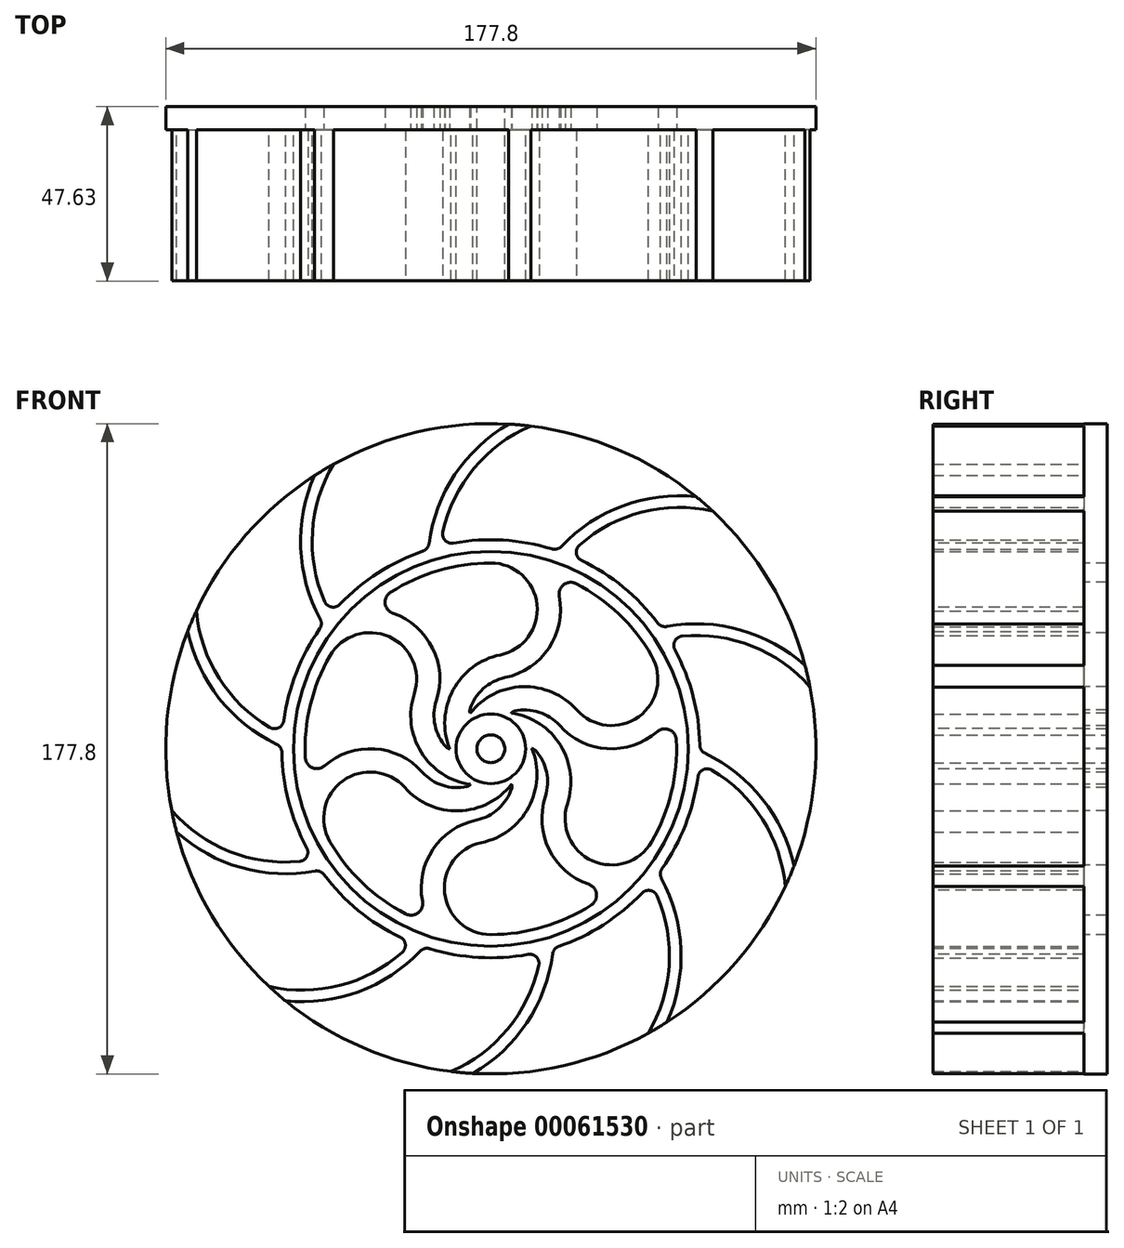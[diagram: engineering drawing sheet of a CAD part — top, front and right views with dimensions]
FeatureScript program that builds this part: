
annotation { "Feature Type Name" : "Feature", "Feature Type Description" : "" }
export const myFeature = defineFeature(function(context is Context, id is Id, definition is map)
    precondition{}
    {
        {
            var Q0;
            Q0=qCreatedBy(makeId("Front.planeOp"),FACE);
            var sketch = newSketch(context, id + "F0", { "sketchPlane" : qUnion([Q0])});
            skCircle(sketch, "E0", {"center": v(0, 0) * mm, "radius": 88.9 * mm});
            skSolve(sketch);
        }
        {
            var Q0;
            Q0=makeQuery(id+"F0.imprint","IMPRINT",FACE,{"disambiguationData":[TD([[makeQuery(id+"F0.imprint","IMPRINT",EDGE,{"derivedFrom":sQuery(id+"F0.wireOp",EDGE,"E0")}),1.0]])]});
            extrude(context, id + "F1", {"entities" : qUnion([Q0]), "depth" : 6.35 * mm});
        }
        {
            var Q0;
            Q0=makeQuery(id+"F1.opExtrude","CAP_FACE",FACE,{"disambiguationData":[OSD([sQuery(id+"F0.wireOp",EDGE,"E0")])],"isStart":false});
            var sketch = newSketch(context, id + "F2", { "sketchPlane" : qUnion([Q0])});
            skCircle(sketch, "E1", {"center": v(0, 0) * mm, "radius": 57.15 * mm});
            skCircle(sketch, "E2", {"center": v(0, 0) * mm, "radius": 53.98 * mm});
            skSolve(sketch);
        }
        {
            var Q0;
            Q0 = qSketchRegion(id + "F2", true);
            extrude(context, id + "F3", {"entities" : qUnion([Q0]), "operationType" : NewBodyOperationType.ADD, "depth" : 41.27 * mm});
        }
        {
            var Q0;
            {var subQ0=sQuery(id+"F0.wireOp",EDGE,"E0");Q0=makeQuery(id+"F3.boolean.opBoolean","SPLIT",FACE,{"disambiguationData":[TD([makeQuery(id+"F1.opExtrude","SWEPT_FACE",FACE,{"disambiguationData":[OSD([subQ0])]})])],"derivedFrom":makeQuery(id+"F1.opExtrude","CAP_FACE",FACE,{"disambiguationData":[OSD([subQ0])],"isStart":false})});}
            var sketch = newSketch(context, id + "F4", { "sketchPlane" : qUnion([Q0])});
            skArc(sketch, "E3", {"start": v(80.54, -37.63) * mm, "mid": v(72.26, -16.34) * mm, "end": v(53.9, -2.7) * mm});
            skArc(sketch, "E4", {"start": v(82.9, -32.09) * mm, "mid": v(72.74, -11.92) * mm, "end": v(53.97, 0.64) * mm});
            skArc(sketch, "E5.0", {"start": v(53.9, -2.7) * mm, "mid": v(53.97, -1.03) * mm, "end": v(53.97, 0.64) * mm});
            skArc(sketch, "E6.0", {"start": v(80.54, -37.63) * mm, "mid": v(81.77, -34.88) * mm, "end": v(82.9, -32.09) * mm});
            skArc(sketch, "E7.1.0", {"start": v(87.28, 16.9) * mm, "mid": v(68.06, 29.26) * mm, "end": v(45.2, 29.5) * mm});
            skArc(sketch, "E7.1.1", {"start": v(85.93, 22.77) * mm, "mid": v(65.85, 33.1) * mm, "end": v(43.29, 32.24) * mm});
            skArc(sketch, "E7.1.2", {"start": v(87.28, 16.9) * mm, "mid": v(86.66, 19.84) * mm, "end": v(85.93, 22.77) * mm});
            skArc(sketch, "E7.1.3", {"start": v(45.2, 29.5) * mm, "mid": v(44.27, 30.88) * mm, "end": v(43.29, 32.24) * mm});
            skArc(sketch, "E7.2.0", {"start": v(60.68, 64.97) * mm, "mid": v(37.86, 63.67) * mm, "end": v(19.24, 50.43) * mm});
            skArc(sketch, "E7.2.1", {"start": v(56.14, 68.93) * mm, "mid": v(33.82, 65.5) * mm, "end": v(16.07, 51.53) * mm});
            skArc(sketch, "E7.2.2", {"start": v(60.68, 64.97) * mm, "mid": v(58.44, 66.99) * mm, "end": v(56.14, 68.93) * mm});
            skArc(sketch, "E7.2.3", {"start": v(19.24, 50.43) * mm, "mid": v(17.66, 51) * mm, "end": v(16.07, 51.53) * mm});
            skArc(sketch, "E7.3.0", {"start": v(10.9, 88.23) * mm, "mid": v(-6.8, 73.77) * mm, "end": v(-14.08, 52.1) * mm});
            skArc(sketch, "E7.3.1", {"start": v(4.9, 88.76) * mm, "mid": v(-11.14, 72.86) * mm, "end": v(-17.29, 51.13) * mm});
            skArc(sketch, "E7.3.2", {"start": v(10.9, 88.23) * mm, "mid": v(7.9, 88.55) * mm, "end": v(4.9, 88.76) * mm});
            skArc(sketch, "E7.3.3", {"start": v(-14.08, 52.1) * mm, "mid": v(-15.7, 51.64) * mm, "end": v(-17.29, 51.13) * mm});
            skArc(sketch, "E7.4.0", {"start": v(-43.04, 77.79) * mm, "mid": v(-48.85, 55.69) * mm, "end": v(-42.02, 33.88) * mm});
            skArc(sketch, "E7.4.1", {"start": v(-48.21, 74.7) * mm, "mid": v(-51.84, 52.4) * mm, "end": v(-44.04, 31.2) * mm});
            skArc(sketch, "E7.4.2", {"start": v(-43.04, 77.79) * mm, "mid": v(-45.65, 76.28) * mm, "end": v(-48.21, 74.7) * mm});
            skArc(sketch, "E7.4.3", {"start": v(-42.02, 33.88) * mm, "mid": v(-43.05, 32.56) * mm, "end": v(-44.04, 31.2) * mm});
            skArc(sketch, "E7.5.0", {"start": v(-80.54, 37.63) * mm, "mid": v(-72.26, 16.34) * mm, "end": v(-53.9, 2.7) * mm});
            skArc(sketch, "E7.5.1", {"start": v(-82.9, 32.09) * mm, "mid": v(-72.74, 11.92) * mm, "end": v(-53.97, -0.64) * mm});
            skArc(sketch, "E7.5.2", {"start": v(-80.54, 37.63) * mm, "mid": v(-81.77, 34.88) * mm, "end": v(-82.9, 32.09) * mm});
            skArc(sketch, "E7.5.3", {"start": v(-53.9, 2.7) * mm, "mid": v(-53.97, 1.03) * mm, "end": v(-53.97, -0.64) * mm});
            skArc(sketch, "E7.6.0", {"start": v(-87.28, -16.9) * mm, "mid": v(-68.06, -29.26) * mm, "end": v(-45.2, -29.5) * mm});
            skArc(sketch, "E7.6.1", {"start": v(-85.93, -22.77) * mm, "mid": v(-65.85, -33.1) * mm, "end": v(-43.29, -32.24) * mm});
            skArc(sketch, "E7.6.2", {"start": v(-87.28, -16.9) * mm, "mid": v(-86.66, -19.84) * mm, "end": v(-85.93, -22.77) * mm});
            skArc(sketch, "E7.6.3", {"start": v(-45.2, -29.5) * mm, "mid": v(-44.27, -30.88) * mm, "end": v(-43.29, -32.24) * mm});
            skArc(sketch, "E7.7.0", {"start": v(-60.68, -64.97) * mm, "mid": v(-37.86, -63.67) * mm, "end": v(-19.24, -50.43) * mm});
            skArc(sketch, "E7.7.1", {"start": v(-56.14, -68.93) * mm, "mid": v(-33.82, -65.5) * mm, "end": v(-16.07, -51.53) * mm});
            skArc(sketch, "E7.7.2", {"start": v(-60.68, -64.97) * mm, "mid": v(-58.44, -66.99) * mm, "end": v(-56.14, -68.93) * mm});
            skArc(sketch, "E7.7.3", {"start": v(-19.24, -50.43) * mm, "mid": v(-17.66, -51) * mm, "end": v(-16.07, -51.53) * mm});
            skArc(sketch, "E7.8.0", {"start": v(-10.9, -88.23) * mm, "mid": v(6.8, -73.77) * mm, "end": v(14.08, -52.1) * mm});
            skArc(sketch, "E7.8.1", {"start": v(-4.9, -88.76) * mm, "mid": v(11.14, -72.86) * mm, "end": v(17.29, -51.13) * mm});
            skArc(sketch, "E7.8.2", {"start": v(-10.9, -88.23) * mm, "mid": v(-7.9, -88.55) * mm, "end": v(-4.9, -88.76) * mm});
            skArc(sketch, "E7.8.3", {"start": v(14.08, -52.1) * mm, "mid": v(15.7, -51.64) * mm, "end": v(17.29, -51.13) * mm});
            skArc(sketch, "E7.9.0", {"start": v(43.04, -77.79) * mm, "mid": v(48.85, -55.69) * mm, "end": v(42.02, -33.88) * mm});
            skArc(sketch, "E7.9.1", {"start": v(48.21, -74.7) * mm, "mid": v(51.84, -52.4) * mm, "end": v(44.04, -31.2) * mm});
            skArc(sketch, "E7.9.2", {"start": v(43.04, -77.79) * mm, "mid": v(45.65, -76.28) * mm, "end": v(48.21, -74.7) * mm});
            skArc(sketch, "E7.9.3", {"start": v(42.02, -33.88) * mm, "mid": v(43.05, -32.56) * mm, "end": v(44.04, -31.2) * mm});
            skSolve(sketch);
        }
        {
            var Q0;
            Q0 = qSketchRegion(id + "F4", true);
            var Q1;
            Q1=makeQuery(id+"F3.opExtrude","CAP_FACE",FACE,{"disambiguationData":[OSD([sQuery(id+"F2.wireOp",EDGE,"E1"),sQuery(id+"F2.wireOp",EDGE,"E2")])],"isStart":false});
            extrude(context, id + "F5", {"entities" : qUnion([Q0]), "operationType" : NewBodyOperationType.ADD, "endBound" : BoundingType.UP_TO_SURFACE, "endBoundEntityFace" : qUnion([Q1]), "depth" : 25.4 * mm});
        }
        {
            var Q0;
            Q0=makeQuery(id+"F3.boolean.opBoolean","SPLIT",FACE,{"disambiguationData":[TD([makeQuery(id+"F3.opExtrude","SWEPT_FACE",FACE,{"disambiguationData":[OSD([sQuery(id+"F2.wireOp",EDGE,"E2")])]})])],"derivedFrom":makeQuery(id+"F1.opExtrude","CAP_FACE",FACE,{"disambiguationData":[OSD([sQuery(id+"F0.wireOp",EDGE,"E0")])],"isStart":false})});
            var sketch = newSketch(context, id + "F6", { "sketchPlane" : qUnion([Q0])});
            skCircle(sketch, "E8", {"center": v(0, 0) * mm, "radius": 3.81 * mm});
            skCircle(sketch, "E9", {"center": v(0, 0) * mm, "radius": 9.53 * mm});
            skSolve(sketch);
        }
        {
            var Q0;
            Q0 = qSketchRegion(id + "F6", true);
            var Q1;
            {var subQ0=sQuery(id+"F2.wireOp",EDGE,"E2");var subQ1=sQuery(id+"F2.wireOp",EDGE,"E1");Q1=makeQuery(id+"F5.boolean.opBoolean","MERGE",FACE,{"derivedFrom":[makeQuery(id+"F3.opExtrude","CAP_FACE",FACE,{"disambiguationData":[OSD([subQ1,subQ0])],"isStart":false}),makeQuery(id+"F5.opExtrude","CAP_FACE",FACE,{"disambiguationData":[OSD([subQ1,subQ0]),ownerDisambiguation([makeQuery(id+"F5.opExtrude","SWEPT_BODY",BODY,{"disambiguationData":[OSD([sQuery(id+"F4.wireOp",EDGE,"E3"),sQuery(id+"F4.wireOp",EDGE,"E4"),sQuery(id+"F4.wireOp",EDGE,"E5.0"),sQuery(id+"F4.wireOp",EDGE,"E6.0")])]})])],"isStart":false}),makeQuery(id+"F5.opExtrude","CAP_FACE",FACE,{"disambiguationData":[OSD([subQ1,subQ0]),ownerDisambiguation([makeQuery(id+"F5.opExtrude","SWEPT_BODY",BODY,{"disambiguationData":[OSD([sQuery(id+"F4.wireOp",EDGE,"E7.1.0"),sQuery(id+"F4.wireOp",EDGE,"E7.1.1"),sQuery(id+"F4.wireOp",EDGE,"E7.1.2"),sQuery(id+"F4.wireOp",EDGE,"E7.1.3")])]})])],"isStart":false}),makeQuery(id+"F5.opExtrude","CAP_FACE",FACE,{"disambiguationData":[OSD([subQ1,subQ0]),ownerDisambiguation([makeQuery(id+"F5.opExtrude","SWEPT_BODY",BODY,{"disambiguationData":[OSD([sQuery(id+"F4.wireOp",EDGE,"E7.2.0"),sQuery(id+"F4.wireOp",EDGE,"E7.2.1"),sQuery(id+"F4.wireOp",EDGE,"E7.2.2"),sQuery(id+"F4.wireOp",EDGE,"E7.2.3")])]})])],"isStart":false}),makeQuery(id+"F5.opExtrude","CAP_FACE",FACE,{"disambiguationData":[OSD([subQ1,subQ0]),ownerDisambiguation([makeQuery(id+"F5.opExtrude","SWEPT_BODY",BODY,{"disambiguationData":[OSD([sQuery(id+"F4.wireOp",EDGE,"E7.3.0"),sQuery(id+"F4.wireOp",EDGE,"E7.3.1"),sQuery(id+"F4.wireOp",EDGE,"E7.3.2"),sQuery(id+"F4.wireOp",EDGE,"E7.3.3")])]})])],"isStart":false}),makeQuery(id+"F5.opExtrude","CAP_FACE",FACE,{"disambiguationData":[OSD([subQ1,subQ0]),ownerDisambiguation([makeQuery(id+"F5.opExtrude","SWEPT_BODY",BODY,{"disambiguationData":[OSD([sQuery(id+"F4.wireOp",EDGE,"E7.4.0"),sQuery(id+"F4.wireOp",EDGE,"E7.4.1"),sQuery(id+"F4.wireOp",EDGE,"E7.4.2"),sQuery(id+"F4.wireOp",EDGE,"E7.4.3")])]})])],"isStart":false}),makeQuery(id+"F5.opExtrude","CAP_FACE",FACE,{"disambiguationData":[OSD([subQ1,subQ0]),ownerDisambiguation([makeQuery(id+"F5.opExtrude","SWEPT_BODY",BODY,{"disambiguationData":[OSD([sQuery(id+"F4.wireOp",EDGE,"E7.5.0"),sQuery(id+"F4.wireOp",EDGE,"E7.5.1"),sQuery(id+"F4.wireOp",EDGE,"E7.5.2"),sQuery(id+"F4.wireOp",EDGE,"E7.5.3")])]})])],"isStart":false}),makeQuery(id+"F5.opExtrude","CAP_FACE",FACE,{"disambiguationData":[OSD([subQ1,subQ0]),ownerDisambiguation([makeQuery(id+"F5.opExtrude","SWEPT_BODY",BODY,{"disambiguationData":[OSD([sQuery(id+"F4.wireOp",EDGE,"E7.6.0"),sQuery(id+"F4.wireOp",EDGE,"E7.6.1"),sQuery(id+"F4.wireOp",EDGE,"E7.6.2"),sQuery(id+"F4.wireOp",EDGE,"E7.6.3")])]})])],"isStart":false}),makeQuery(id+"F5.opExtrude","CAP_FACE",FACE,{"disambiguationData":[OSD([subQ1,subQ0]),ownerDisambiguation([makeQuery(id+"F5.opExtrude","SWEPT_BODY",BODY,{"disambiguationData":[OSD([sQuery(id+"F4.wireOp",EDGE,"E7.7.0"),sQuery(id+"F4.wireOp",EDGE,"E7.7.1"),sQuery(id+"F4.wireOp",EDGE,"E7.7.2"),sQuery(id+"F4.wireOp",EDGE,"E7.7.3")])]})])],"isStart":false}),makeQuery(id+"F5.opExtrude","CAP_FACE",FACE,{"disambiguationData":[OSD([subQ1,subQ0]),ownerDisambiguation([makeQuery(id+"F5.opExtrude","SWEPT_BODY",BODY,{"disambiguationData":[OSD([sQuery(id+"F4.wireOp",EDGE,"E7.8.0"),sQuery(id+"F4.wireOp",EDGE,"E7.8.1"),sQuery(id+"F4.wireOp",EDGE,"E7.8.2"),sQuery(id+"F4.wireOp",EDGE,"E7.8.3")])]})])],"isStart":false}),makeQuery(id+"F5.opExtrude","CAP_FACE",FACE,{"disambiguationData":[OSD([subQ1,subQ0]),ownerDisambiguation([makeQuery(id+"F5.opExtrude","SWEPT_BODY",BODY,{"disambiguationData":[OSD([sQuery(id+"F4.wireOp",EDGE,"E7.9.0"),sQuery(id+"F4.wireOp",EDGE,"E7.9.1"),sQuery(id+"F4.wireOp",EDGE,"E7.9.2"),sQuery(id+"F4.wireOp",EDGE,"E7.9.3")])]})])],"isStart":false})]});}
            extrude(context, id + "F7", {"entities" : qUnion([Q0]), "operationType" : NewBodyOperationType.ADD, "endBound" : BoundingType.UP_TO_SURFACE, "endBoundEntityFace" : qUnion([Q1]), "depth" : 25.4 * mm});
        }
        {
            var Q0;
            {var subQ0=makeQuery(id+"F3.opExtrude","SWEPT_FACE",FACE,{"disambiguationData":[OSD([sQuery(id+"F2.wireOp",EDGE,"E2")])]});Q0=makeQuery(id+"F7.boolean.opBoolean","SPLIT",FACE,{"disambiguationData":[TD([subQ0])],"derivedFrom":makeQuery(id+"F3.boolean.opBoolean","SPLIT",FACE,{"disambiguationData":[TD([subQ0])],"derivedFrom":makeQuery(id+"F1.opExtrude","CAP_FACE",FACE,{"disambiguationData":[OSD([sQuery(id+"F0.wireOp",EDGE,"E0")])],"isStart":false})})});}
            var sketch = newSketch(context, id + "F8", { "sketchPlane" : qUnion([Q0])});
            skCircle(sketch, "E10.0", {"center": v(0, 0) * mm, "radius": 3.81 * mm});
            skArc(sketch, "E11", {"start": v(0, 50.8) * mm, "mid": v(-14.31, 48.74) * mm, "end": v(-27.47, 42.73) * mm, "construction": true});
            skArc(sketch, "E12", {"start": v(3.87, 19.45) * mm, "mid": v(-2.1, 16.41) * mm, "end": v(-5.68, 10.77) * mm});
            skArc(sketch, "E13", {"start": v(2.58, 25.66) * mm, "mid": v(-10.33, 16.04) * mm, "end": v(-11.26, -0.03) * mm});
            skArc(sketch, "E14", {"start": v(2.58, 25.66) * mm, "mid": v(12.63, 39.4) * mm, "end": v(0, 50.8) * mm});
            skArc(sketch, "E15", {"start": v(3.87, 19.45) * mm, "mid": v(15.86, 27.54) * mm, "end": v(18.7, 41.73) * mm});
            skPoint(sketch, "E16.visualSharp", {"position": v(16.18, 48.15) * mm});
            skArc(sketch, "E16.filletArc", {"start": v(23.27, 45.16) * mm, "mid": v(19.91, 44.87) * mm, "end": v(18.7, 41.73) * mm});
            skPoint(sketch, "E17.visualSharp", {"position": v(-6.25, 7.19) * mm});
            skArc(sketch, "E17.filletArc", {"start": v(-5.68, 10.77) * mm, "mid": v(-5.75, 10.25) * mm, "end": v(-5.65, 9.73) * mm});
            skPoint(sketch, "E18.1.1", {"position": v(-33.61, 38.1) * mm});
            skArc(sketch, "E18.1.2", {"start": v(-14.9, 13.07) * mm, "mid": v(-15.26, 6.4) * mm, "end": v(-12.17, 0.46) * mm});
            skArc(sketch, "E18.1.3", {"start": v(-20.94, 15.07) * mm, "mid": v(-27.8, 30.64) * mm, "end": v(-44, 25.4) * mm});
            skArc(sketch, "E18.1.4", {"start": v(-20.94, 15.07) * mm, "mid": v(-19.06, -0.92) * mm, "end": v(-5.6, -9.76) * mm});
            skPoint(sketch, "E18.1.5", {"position": v(-9.35, -1.82) * mm});
            skArc(sketch, "E18.1.6", {"start": v(-14.9, 13.07) * mm, "mid": v(-15.92, 27.5) * mm, "end": v(-26.79, 37.06) * mm});
            skArc(sketch, "E18.1.7", {"start": v(-27.47, 42.73) * mm, "mid": v(-28.9, 39.68) * mm, "end": v(-26.79, 37.06) * mm});
            skArc(sketch, "E18.1.8", {"start": v(-12.17, 0.46) * mm, "mid": v(-11.75, 0.14) * mm, "end": v(-11.26, -0.03) * mm});
            skPoint(sketch, "E18.2.1", {"position": v(-49.8, -10.06) * mm});
            skArc(sketch, "E18.2.2", {"start": v(-18.78, -6.37) * mm, "mid": v(-13.17, -10.02) * mm, "end": v(-6.49, -10.3) * mm});
            skArc(sketch, "E18.2.3", {"start": v(-23.52, -10.6) * mm, "mid": v(-40.43, -8.76) * mm, "end": v(-44, -25.4) * mm});
            skArc(sketch, "E18.2.4", {"start": v(-23.52, -10.6) * mm, "mid": v(-8.73, -16.96) * mm, "end": v(5.65, -9.73) * mm});
            skPoint(sketch, "E18.2.5", {"position": v(-3.1, -9) * mm});
            skArc(sketch, "E18.2.6", {"start": v(-18.78, -6.37) * mm, "mid": v(-31.78, -0.04) * mm, "end": v(-45.49, -4.67) * mm});
            skArc(sketch, "E18.2.7", {"start": v(-50.74, -2.42) * mm, "mid": v(-48.82, -5.2) * mm, "end": v(-45.49, -4.67) * mm});
            skArc(sketch, "E18.2.8", {"start": v(-6.49, -10.3) * mm, "mid": v(-6, -10.1) * mm, "end": v(-5.6, -9.76) * mm});
            skPoint(sketch, "E18.3.1", {"position": v(-16.18, -48.15) * mm});
            skArc(sketch, "E18.3.2", {"start": v(-3.87, -19.45) * mm, "mid": v(2.1, -16.41) * mm, "end": v(5.68, -10.77) * mm});
            skArc(sketch, "E18.3.3", {"start": v(-2.58, -25.66) * mm, "mid": v(-12.63, -39.4) * mm, "end": v(0, -50.8) * mm});
            skArc(sketch, "E18.3.4", {"start": v(-2.58, -25.66) * mm, "mid": v(10.33, -16.04) * mm, "end": v(11.26, 0.03) * mm});
            skPoint(sketch, "E18.3.5", {"position": v(6.25, -7.19) * mm});
            skArc(sketch, "E18.3.6", {"start": v(-3.87, -19.45) * mm, "mid": v(-15.86, -27.54) * mm, "end": v(-18.7, -41.73) * mm});
            skArc(sketch, "E18.3.7", {"start": v(-23.27, -45.16) * mm, "mid": v(-19.91, -44.87) * mm, "end": v(-18.7, -41.73) * mm});
            skArc(sketch, "E18.3.8", {"start": v(5.68, -10.77) * mm, "mid": v(5.75, -10.25) * mm, "end": v(5.65, -9.73) * mm});
            skPoint(sketch, "E18.4.1", {"position": v(33.61, -38.1) * mm});
            skArc(sketch, "E18.4.2", {"start": v(14.9, -13.07) * mm, "mid": v(15.26, -6.4) * mm, "end": v(12.17, -0.46) * mm});
            skArc(sketch, "E18.4.3", {"start": v(20.94, -15.07) * mm, "mid": v(27.8, -30.64) * mm, "end": v(44, -25.4) * mm});
            skArc(sketch, "E18.4.4", {"start": v(20.94, -15.07) * mm, "mid": v(19.06, 0.92) * mm, "end": v(5.6, 9.76) * mm});
            skPoint(sketch, "E18.4.5", {"position": v(9.35, 1.82) * mm});
            skArc(sketch, "E18.4.6", {"start": v(14.9, -13.07) * mm, "mid": v(15.92, -27.5) * mm, "end": v(26.79, -37.06) * mm});
            skArc(sketch, "E18.4.7", {"start": v(27.47, -42.73) * mm, "mid": v(28.9, -39.68) * mm, "end": v(26.79, -37.06) * mm});
            skArc(sketch, "E18.4.8", {"start": v(12.17, -0.46) * mm, "mid": v(11.75, -0.14) * mm, "end": v(11.26, 0.03) * mm});
            skPoint(sketch, "E18.5.1", {"position": v(49.8, 10.06) * mm});
            skArc(sketch, "E18.5.2", {"start": v(18.78, 6.37) * mm, "mid": v(13.17, 10.02) * mm, "end": v(6.49, 10.3) * mm});
            skArc(sketch, "E18.5.3", {"start": v(23.52, 10.6) * mm, "mid": v(40.43, 8.76) * mm, "end": v(44, 25.4) * mm});
            skArc(sketch, "E18.5.4", {"start": v(23.52, 10.6) * mm, "mid": v(8.73, 16.96) * mm, "end": v(-5.65, 9.73) * mm});
            skPoint(sketch, "E18.5.5", {"position": v(3.1, 9) * mm});
            skArc(sketch, "E18.5.6", {"start": v(18.78, 6.37) * mm, "mid": v(31.78, 0.04) * mm, "end": v(45.49, 4.67) * mm});
            skArc(sketch, "E18.5.7", {"start": v(50.74, 2.42) * mm, "mid": v(48.82, 5.2) * mm, "end": v(45.49, 4.67) * mm});
            skArc(sketch, "E18.5.8", {"start": v(6.49, 10.3) * mm, "mid": v(6, 10.1) * mm, "end": v(5.6, 9.76) * mm});
            skArc(sketch, "E19", {"start": v(44, 25.4) * mm, "mid": v(35.05, 36.77) * mm, "end": v(23.27, 45.16) * mm});
            skArc(sketch, "E20.trimOffspring", {"start": v(44, -25.4) * mm, "mid": v(49.37, -11.97) * mm, "end": v(50.74, 2.42) * mm});
            skArc(sketch, "E21.trimOffspring", {"start": v(0, 50.8) * mm, "mid": v(-14.31, 48.74) * mm, "end": v(-27.47, 42.73) * mm});
            skArc(sketch, "E22.trimOffspring", {"start": v(44, 25.4) * mm, "mid": v(35.05, 36.77) * mm, "end": v(23.27, 45.16) * mm, "construction": true});
            skArc(sketch, "E23.trimOffspring", {"start": v(44, -25.4) * mm, "mid": v(49.37, -11.97) * mm, "end": v(50.74, 2.42) * mm, "construction": true});
            skArc(sketch, "E24.trimOffspring", {"start": v(0, -50.8) * mm, "mid": v(14.31, -48.74) * mm, "end": v(27.47, -42.73) * mm});
            skArc(sketch, "E25.trimOffspring", {"start": v(0, -50.8) * mm, "mid": v(14.31, -48.74) * mm, "end": v(27.47, -42.73) * mm, "construction": true});
            skArc(sketch, "E26.trimOffspring", {"start": v(-44, 25.4) * mm, "mid": v(-49.37, 11.97) * mm, "end": v(-50.74, -2.42) * mm});
            skArc(sketch, "E27.trimOffspring", {"start": v(-44, -25.4) * mm, "mid": v(-35.05, -36.77) * mm, "end": v(-23.27, -45.16) * mm});
            skArc(sketch, "E28.trimOffspring", {"start": v(-44, -25.4) * mm, "mid": v(-35.05, -36.77) * mm, "end": v(-23.27, -45.16) * mm, "construction": true});
            skArc(sketch, "E29.trimOffspring", {"start": v(-44, 25.4) * mm, "mid": v(-49.37, 11.97) * mm, "end": v(-50.74, -2.42) * mm, "construction": true});
            skPoint(sketch, "E30.orphan", {"position": v(9.43, -1.32) * mm});
            skPoint(sketch, "E31.orphan", {"position": v(5.86, 7.5) * mm});
            skPoint(sketch, "E32.orphan", {"position": v(-3.57, 8.83) * mm});
            skPoint(sketch, "E33.orphan", {"position": v(-9.43, 1.32) * mm});
            skPoint(sketch, "E34.orphan", {"position": v(-5.86, -7.5) * mm});
            skPoint(sketch, "E35.orphan", {"position": v(3.57, -8.83) * mm});
            skSolve(sketch);
        }
        {
            var Q0;
            Q0 = qSketchRegion(id + "F8", true);
            extrude(context, id + "F9", {"entities" : qUnion([Q0]), "operationType" : NewBodyOperationType.REMOVE, "oppositeDirection" : true, "depth" : 25.4 * mm});
        }
        {
            var Q0;
            Q0=makeQuery(id+"F5.boolean.opBoolean","INTERSECT",EDGE,{"derivedFrom":[makeQuery(id+"F3.opExtrude","SWEPT_FACE",FACE,{"disambiguationData":[OSD([sQuery(id+"F2.wireOp",EDGE,"E1")])]}),makeQuery(id+"F5.opExtrude","SWEPT_FACE",FACE,{"disambiguationData":[OSD([sQuery(id+"F4.wireOp",EDGE,"E7.1.0")])]})]});
            var Q1;
            Q1=makeQuery(id+"F5.boolean.opBoolean","INTERSECT",EDGE,{"derivedFrom":[makeQuery(id+"F3.opExtrude","SWEPT_FACE",FACE,{"disambiguationData":[OSD([sQuery(id+"F2.wireOp",EDGE,"E1")])]}),makeQuery(id+"F5.opExtrude","SWEPT_FACE",FACE,{"disambiguationData":[OSD([sQuery(id+"F4.wireOp",EDGE,"E4")])]})]});
            var Q2;
            Q2=makeQuery(id+"F5.boolean.opBoolean","INTERSECT",EDGE,{"derivedFrom":[makeQuery(id+"F3.opExtrude","SWEPT_FACE",FACE,{"disambiguationData":[OSD([sQuery(id+"F2.wireOp",EDGE,"E1")])]}),makeQuery(id+"F5.opExtrude","SWEPT_FACE",FACE,{"disambiguationData":[OSD([sQuery(id+"F4.wireOp",EDGE,"E3")])]})]});
            var Q3;
            Q3=makeQuery(id+"F5.boolean.opBoolean","INTERSECT",EDGE,{"derivedFrom":[makeQuery(id+"F3.opExtrude","SWEPT_FACE",FACE,{"disambiguationData":[OSD([sQuery(id+"F2.wireOp",EDGE,"E1")])]}),makeQuery(id+"F5.opExtrude","SWEPT_FACE",FACE,{"disambiguationData":[OSD([sQuery(id+"F4.wireOp",EDGE,"E7.9.1")])]})]});
            var Q4;
            Q4=makeQuery(id+"F5.boolean.opBoolean","INTERSECT",EDGE,{"derivedFrom":[makeQuery(id+"F3.opExtrude","SWEPT_FACE",FACE,{"disambiguationData":[OSD([sQuery(id+"F2.wireOp",EDGE,"E1")])]}),makeQuery(id+"F5.opExtrude","SWEPT_FACE",FACE,{"disambiguationData":[OSD([sQuery(id+"F4.wireOp",EDGE,"E7.9.0")])]})]});
            var Q5;
            Q5=makeQuery(id+"F5.boolean.opBoolean","INTERSECT",EDGE,{"derivedFrom":[makeQuery(id+"F3.opExtrude","SWEPT_FACE",FACE,{"disambiguationData":[OSD([sQuery(id+"F2.wireOp",EDGE,"E1")])]}),makeQuery(id+"F5.opExtrude","SWEPT_FACE",FACE,{"disambiguationData":[OSD([sQuery(id+"F4.wireOp",EDGE,"E7.8.1")])]})]});
            var Q6;
            Q6=makeQuery(id+"F5.boolean.opBoolean","INTERSECT",EDGE,{"derivedFrom":[makeQuery(id+"F3.opExtrude","SWEPT_FACE",FACE,{"disambiguationData":[OSD([sQuery(id+"F2.wireOp",EDGE,"E1")])]}),makeQuery(id+"F5.opExtrude","SWEPT_FACE",FACE,{"disambiguationData":[OSD([sQuery(id+"F4.wireOp",EDGE,"E7.8.0")])]})]});
            var Q7;
            Q7=makeQuery(id+"F5.boolean.opBoolean","INTERSECT",EDGE,{"derivedFrom":[makeQuery(id+"F3.opExtrude","SWEPT_FACE",FACE,{"disambiguationData":[OSD([sQuery(id+"F2.wireOp",EDGE,"E1")])]}),makeQuery(id+"F5.opExtrude","SWEPT_FACE",FACE,{"disambiguationData":[OSD([sQuery(id+"F4.wireOp",EDGE,"E7.7.1")])]})]});
            var Q8;
            Q8=makeQuery(id+"F5.boolean.opBoolean","INTERSECT",EDGE,{"derivedFrom":[makeQuery(id+"F3.opExtrude","SWEPT_FACE",FACE,{"disambiguationData":[OSD([sQuery(id+"F2.wireOp",EDGE,"E1")])]}),makeQuery(id+"F5.opExtrude","SWEPT_FACE",FACE,{"disambiguationData":[OSD([sQuery(id+"F4.wireOp",EDGE,"E7.6.1")])]})]});
            var Q9;
            Q9=makeQuery(id+"F5.boolean.opBoolean","INTERSECT",EDGE,{"derivedFrom":[makeQuery(id+"F3.opExtrude","SWEPT_FACE",FACE,{"disambiguationData":[OSD([sQuery(id+"F2.wireOp",EDGE,"E1")])]}),makeQuery(id+"F5.opExtrude","SWEPT_FACE",FACE,{"disambiguationData":[OSD([sQuery(id+"F4.wireOp",EDGE,"E7.7.0")])]})]});
            var Q10;
            Q10=makeQuery(id+"F5.boolean.opBoolean","INTERSECT",EDGE,{"derivedFrom":[makeQuery(id+"F3.opExtrude","SWEPT_FACE",FACE,{"disambiguationData":[OSD([sQuery(id+"F2.wireOp",EDGE,"E1")])]}),makeQuery(id+"F5.opExtrude","SWEPT_FACE",FACE,{"disambiguationData":[OSD([sQuery(id+"F4.wireOp",EDGE,"E7.6.0")])]})]});
            var Q11;
            Q11=makeQuery(id+"F5.boolean.opBoolean","INTERSECT",EDGE,{"derivedFrom":[makeQuery(id+"F3.opExtrude","SWEPT_FACE",FACE,{"disambiguationData":[OSD([sQuery(id+"F2.wireOp",EDGE,"E1")])]}),makeQuery(id+"F5.opExtrude","SWEPT_FACE",FACE,{"disambiguationData":[OSD([sQuery(id+"F4.wireOp",EDGE,"E7.5.0")])]})]});
            var Q12;
            Q12=makeQuery(id+"F5.boolean.opBoolean","INTERSECT",EDGE,{"derivedFrom":[makeQuery(id+"F3.opExtrude","SWEPT_FACE",FACE,{"disambiguationData":[OSD([sQuery(id+"F2.wireOp",EDGE,"E1")])]}),makeQuery(id+"F5.opExtrude","SWEPT_FACE",FACE,{"disambiguationData":[OSD([sQuery(id+"F4.wireOp",EDGE,"E7.4.1")])]})]});
            var Q13;
            Q13=makeQuery(id+"F5.boolean.opBoolean","INTERSECT",EDGE,{"derivedFrom":[makeQuery(id+"F3.opExtrude","SWEPT_FACE",FACE,{"disambiguationData":[OSD([sQuery(id+"F2.wireOp",EDGE,"E1")])]}),makeQuery(id+"F5.opExtrude","SWEPT_FACE",FACE,{"disambiguationData":[OSD([sQuery(id+"F4.wireOp",EDGE,"E7.5.1")])]})]});
            var Q14;
            Q14=makeQuery(id+"F5.boolean.opBoolean","INTERSECT",EDGE,{"derivedFrom":[makeQuery(id+"F3.opExtrude","SWEPT_FACE",FACE,{"disambiguationData":[OSD([sQuery(id+"F2.wireOp",EDGE,"E1")])]}),makeQuery(id+"F5.opExtrude","SWEPT_FACE",FACE,{"disambiguationData":[OSD([sQuery(id+"F4.wireOp",EDGE,"E7.4.0")])]})]});
            var Q15;
            Q15=makeQuery(id+"F5.boolean.opBoolean","INTERSECT",EDGE,{"derivedFrom":[makeQuery(id+"F3.opExtrude","SWEPT_FACE",FACE,{"disambiguationData":[OSD([sQuery(id+"F2.wireOp",EDGE,"E1")])]}),makeQuery(id+"F5.opExtrude","SWEPT_FACE",FACE,{"disambiguationData":[OSD([sQuery(id+"F4.wireOp",EDGE,"E7.3.1")])]})]});
            var Q16;
            Q16=makeQuery(id+"F5.boolean.opBoolean","INTERSECT",EDGE,{"derivedFrom":[makeQuery(id+"F3.opExtrude","SWEPT_FACE",FACE,{"disambiguationData":[OSD([sQuery(id+"F2.wireOp",EDGE,"E1")])]}),makeQuery(id+"F5.opExtrude","SWEPT_FACE",FACE,{"disambiguationData":[OSD([sQuery(id+"F4.wireOp",EDGE,"E7.3.0")])]})]});
            var Q17;
            Q17=makeQuery(id+"F5.boolean.opBoolean","INTERSECT",EDGE,{"derivedFrom":[makeQuery(id+"F3.opExtrude","SWEPT_FACE",FACE,{"disambiguationData":[OSD([sQuery(id+"F2.wireOp",EDGE,"E1")])]}),makeQuery(id+"F5.opExtrude","SWEPT_FACE",FACE,{"disambiguationData":[OSD([sQuery(id+"F4.wireOp",EDGE,"E7.2.1")])]})]});
            var Q18;
            Q18=makeQuery(id+"F5.boolean.opBoolean","INTERSECT",EDGE,{"derivedFrom":[makeQuery(id+"F3.opExtrude","SWEPT_FACE",FACE,{"disambiguationData":[OSD([sQuery(id+"F2.wireOp",EDGE,"E1")])]}),makeQuery(id+"F5.opExtrude","SWEPT_FACE",FACE,{"disambiguationData":[OSD([sQuery(id+"F4.wireOp",EDGE,"E7.2.0")])]})]});
            var Q19;
            Q19=makeQuery(id+"F5.boolean.opBoolean","INTERSECT",EDGE,{"derivedFrom":[makeQuery(id+"F3.opExtrude","SWEPT_FACE",FACE,{"disambiguationData":[OSD([sQuery(id+"F2.wireOp",EDGE,"E1")])]}),makeQuery(id+"F5.opExtrude","SWEPT_FACE",FACE,{"disambiguationData":[OSD([sQuery(id+"F4.wireOp",EDGE,"E7.1.1")])]})]});
            fillet(context, id + "F10", {"entities" : qUnion([Q0, Q1, Q2, Q3, Q4, Q5, Q6, Q7, Q8, Q9, Q10, Q11, Q12, Q13, Q14, Q15, Q16, Q17, Q18, Q19]), "radius" : 2.54 * mm, "tangentPropagation" : true, "allowEdgeOverflow" : false});
        }
    });
